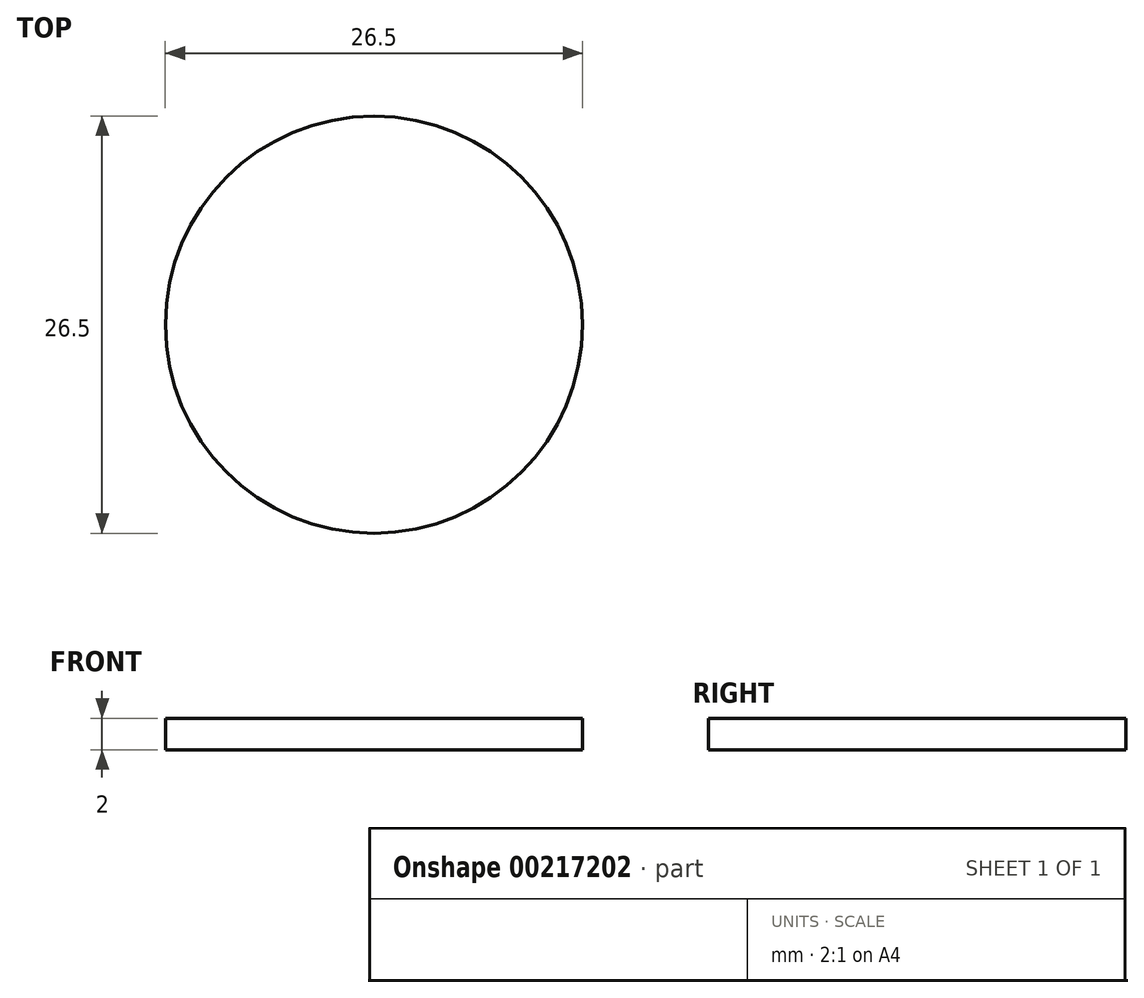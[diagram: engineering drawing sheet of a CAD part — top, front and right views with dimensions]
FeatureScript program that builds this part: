
annotation { "Feature Type Name" : "Feature", "Feature Type Description" : "" }
export const myFeature = defineFeature(function(context is Context, id is Id, definition is map)
    precondition{}
    {
        {
            var Q0;
            Q0=qCreatedBy(makeId("Top.planeOp"),FACE);
            var sketch = newSketch(context, id + "F0", { "sketchPlane" : qUnion([Q0])});
            skCircle(sketch, "E0", {"center": v(0, 0) * mm, "radius": 13.25 * mm});
            skSolve(sketch);
        }
        {
            var Q0;
            Q0=qSketchRegion(id+"F0",true);
            extrude(context, id + "F1", {"entities" : qUnion([Q0]), "endBound" : BoundingType.SYMMETRIC, "depth" : 2 * mm});
        }
    });
